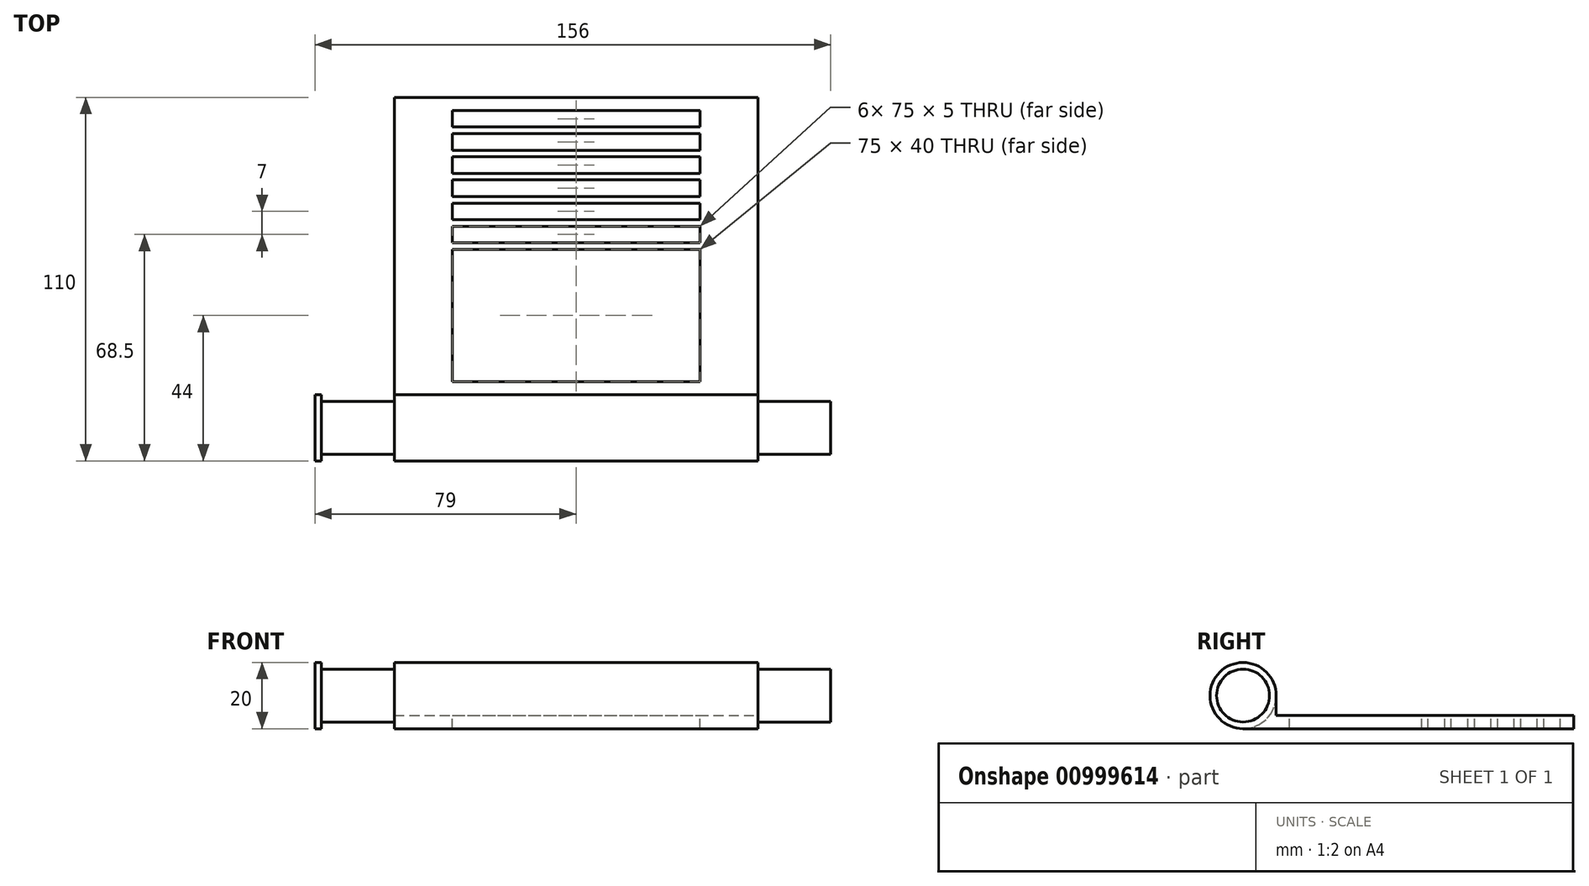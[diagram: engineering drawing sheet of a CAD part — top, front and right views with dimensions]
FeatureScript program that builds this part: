
annotation { "Feature Type Name" : "Feature", "Feature Type Description" : "" }
export const myFeature = defineFeature(function(context is Context, id is Id, definition is map)
    precondition{}
    {
        {
            var Q0;
            Q0=qCreatedBy(makeId("Top.planeOp"),FACE);
            var sketch = newSketch(context, id + "F0", { "sketchPlane" : qUnion([Q0])});
            skLineSegment(sketch, "E0.bottom", {"start": v(75, -45) * mm, "end": v(-75, -45) * mm});
            skLineSegment(sketch, "E0.top", {"start": v(75, 45) * mm, "end": v(-75, 45) * mm});
            skLineSegment(sketch, "E0.left", {"start": v(75, -45) * mm, "end": v(75, 45) * mm});
            skLineSegment(sketch, "E0.right", {"start": v(-75, -45) * mm, "end": v(-75, 45) * mm});
            skPoint(sketch, "E0.middle", {"position": v(0, 0) * mm});
            skLineSegment(sketch, "E1", {"start": v(-75, -45) * mm, "end": v(-75, -65) * mm});
            skLineSegment(sketch, "E2", {"start": v(-75, -65) * mm, "end": v(75, -65) * mm});
            skLineSegment(sketch, "E3", {"start": v(75, -65) * mm, "end": v(75, -45) * mm});
            skLineSegment(sketch, "E4", {"start": v(-55, -45) * mm, "end": v(-55, -65) * mm});
            skLineSegment(sketch, "E5", {"start": v(55, -45) * mm, "end": v(55, -65) * mm});
            skLineSegment(sketch, "E6", {"start": v(-55, -45) * mm, "end": v(-55, 45) * mm});
            skLineSegment(sketch, "E7", {"start": v(55, -45) * mm, "end": v(55, 45) * mm});
            skSolve(sketch);
        }
        {
            var Q0;
            {var subQ0=sQuery(id+"F0.wireOp",EDGE,"E4");Q0=makeQuery(id+"F0.imprint","IMPRINT",FACE,{"disambiguationData":[TD([[makeQuery(id+"F0.imprint","IMPRINT",EDGE,{"derivedFrom":subQ0}),1.0]])]});}
            var Q1;
            {var subQ0=sQuery(id+"F0.wireOp",EDGE,"E6");Q1=makeQuery(id+"F0.imprint","IMPRINT",FACE,{"disambiguationData":[TD([[makeQuery(id+"F0.imprint","IMPRINT",EDGE,{"derivedFrom":subQ0}),-1.0]])]});}
            extrude(context, id + "F1", {"entities" : qUnion([Q0, Q1]), "depth" : 4 * mm, "offsetDistance" : 25 * mm});
        }
        {
            var Q0;
            {var subQ0=sQuery(id+"F0.wireOp",EDGE,"E4");Q0=makeQuery(id+"F0.imprint","IMPRINT",FACE,{"disambiguationData":[TD([[makeQuery(id+"F0.imprint","IMPRINT",EDGE,{"derivedFrom":subQ0}),1.0]])]});}
            extrude(context, id + "F2", {"entities" : qUnion([Q0]), "operationType" : NewBodyOperationType.ADD, "depth" : 20 * mm, "offsetDistance" : 25 * mm});
        }
        {
            var Q0;
            Q0=qCreatedBy(makeId("Right.planeOp"),FACE);
            var sketch = newSketch(context, id + "F3", { "sketchPlane" : qUnion([Q0])});
            skLineSegment(sketch, "E8.0.0", {"start": v(-65, 0) * mm, "end": v(-65, 0) * mm});
            skLineSegment(sketch, "E8.0.1", {"start": v(-65, 0) * mm, "end": v(-65, 20) * mm});
            skLineSegment(sketch, "E8.0.2", {"start": v(-65, 20) * mm, "end": v(-45, 20) * mm});
            skLineSegment(sketch, "E8.0.3", {"start": v(-45, 20) * mm, "end": v(-45, 2) * mm});
            skLineSegment(sketch, "E8.0.4", {"start": v(-65, 0) * mm, "end": v(-65, 2) * mm});
            skPoint(sketch, "E9.centerSnap0", {"position": v(-45, 11) * mm});
            skPoint(sketch, "E9.centerSnap1", {"position": v(-55, 20) * mm});
            skCircle(sketch, "E10", {"center": v(-55, 10) * mm, "radius": 10 * mm});
            skPoint(sketch, "E10.centerSnap0", {"position": v(-65, 10) * mm});
            skCircle(sketch, "E11", {"center": v(-55, 10) * mm, "radius": 8 * mm});
            skLineSegment(sketch, "E12", {"start": v(-65, 0) * mm, "end": v(-41.71, 0) * mm});
            skLineSegment(sketch, "E13", {"start": v(-45, 2) * mm, "end": v(-45, 0) * mm});
            skSolve(sketch);
        }
        {
            var Q0;
            {var subQ0=sQuery(id+"F3.wireOp",EDGE,"E8.0.3");var subQ1=sQuery(id+"F3.wireOp",EDGE,"E8.0.2");var subQ2=makeQuery(id+"F3.imprint","INTERSECT",VERTEX,{"derivedFrom":[subQ1,subQ0]});Q0=makeQuery(id+"F3.imprint","IMPRINT",FACE,{"disambiguationData":[TD([[makeQuery(id+"F3.imprint","IMPRINT",EDGE,{"disambiguationData":[TD([[subQ2,1.0]])],"derivedFrom":subQ1}),-1.0]])]});}
            var Q1;
            {var subQ0=sQuery(id+"F3.wireOp",EDGE,"E10");var subQ1=sQuery(id+"F3.wireOp",EDGE,"E8.0.1");var subQ2=makeQuery(id+"F3.imprint","INTERSECT",VERTEX,{"derivedFrom":[subQ1,subQ0]});Q1=makeQuery(id+"F3.imprint","IMPRINT",FACE,{"disambiguationData":[TD([[makeQuery(id+"F3.imprint","IMPRINT",EDGE,{"disambiguationData":[TD([[subQ2,-1.0]])],"derivedFrom":subQ1}),-1.0]])]});}
            var Q2;
            {var subQ1=sQuery(id+"F3.wireOp",EDGE,"E8.0.1");var subQ3=makeQuery(id+"F3.imprint","IMPRINT",VERTEX,{"derivedFrom":subQ1});Q2=makeQuery(id+"F3.imprint","IMPRINT",FACE,{"disambiguationData":[TD([[makeQuery(id+"F3.imprint","IMPRINT",EDGE,{"disambiguationData":[TD([[subQ3,-1.0]])],"derivedFrom":subQ1}),-1.0]])]});}
            extrude(context, id + "F4", {"entities" : qUnion([Q0, Q1, Q2]), "operationType" : NewBodyOperationType.REMOVE, "endBound" : BoundingType.SYMMETRIC, "oppositeDirection" : true, "depth" : 200 * mm, "offsetDistance" : 25 * mm});
        }
        {
            var Q0;
            Q0=makeQuery(id+"F3.imprint","IMPRINT",FACE,{"disambiguationData":[TD([[makeQuery(id+"F3.imprint","IMPRINT",EDGE,{"derivedFrom":sQuery(id+"F3.wireOp",EDGE,"E11")}),1.0]])]});
            extrude(context, id + "F5", {"entities" : qUnion([Q0]), "operationType" : NewBodyOperationType.ADD, "endBound" : BoundingType.SYMMETRIC, "depth" : 154 * mm, "offsetDistance" : 25 * mm});
        }
        {
            var Q0;
            Q0=makeQuery(id+"F5.opExtrude","CAP_FACE",FACE,{"disambiguationData":[OSD([sQuery(id+"F3.wireOp",EDGE,"E11")])],"isStart":true});
            var sketch = newSketch(context, id + "F6", { "sketchPlane" : qUnion([Q0])});
            skCircle(sketch, "E14", {"center": v(55, 10) * mm, "radius": 10 * mm});
            skSolve(sketch);
        }
        {
            var Q0;
            Q0=makeQuery(id+"F6.imprint","IMPRINT",FACE,{"disambiguationData":[TD([[makeQuery(id+"F6.imprint","IMPRINT",EDGE,{"derivedFrom":sQuery(id+"F6.wireOp",EDGE,"E14")}),1.0]])]});
            var Q1;
            Q1=makeQuery(id+"F6.imprint","IMPRINT",FACE,{"disambiguationData":[TD([[makeQuery(id+"F6.imprint","IMPRINT",EDGE,{"derivedFrom":makeQuery(id+"F5.opExtrude","CAP_EDGE",EDGE,{"disambiguationData":[OSD([sQuery(id+"F3.wireOp",EDGE,"E11")])],"isStart":true})}),-1.0]])]});
            extrude(context, id + "F7", {"entities" : qUnion([Q0, Q1]), "operationType" : NewBodyOperationType.ADD, "depth" : 2 * mm, "offsetDistance" : 25 * mm});
        }
        {
            var Q0;
            Q0=makeQuery(id+"F1.opExtrude","CAP_FACE",FACE,{"disambiguationData":[OSD([sQuery(id+"F0.wireOp",EDGE,"E0.top"),sQuery(id+"F0.wireOp",EDGE,"E2"),sQuery(id+"F0.wireOp",EDGE,"E4"),sQuery(id+"F0.wireOp",EDGE,"E5"),sQuery(id+"F0.wireOp",EDGE,"E6"),sQuery(id+"F0.wireOp",EDGE,"E7")])],"isStart":false});
            var sketch = newSketch(context, id + "F8", { "sketchPlane" : qUnion([Q0])});
            skLineSegment(sketch, "E15", {"start": v(0, 45) * mm, "end": v(0, -45) * mm, "construction": true});
            skLineSegment(sketch, "E16.bottom", {"start": v(-37.5, 36) * mm, "end": v(37.5, 36) * mm});
            skLineSegment(sketch, "E16.top", {"start": v(-37.5, 41) * mm, "end": v(37.5, 41) * mm});
            skLineSegment(sketch, "E16.left", {"start": v(-37.5, 36) * mm, "end": v(-37.5, 41) * mm});
            skLineSegment(sketch, "E16.right", {"start": v(37.5, 36) * mm, "end": v(37.5, 41) * mm});
            skPoint(sketch, "E16.middle", {"position": v(0, 38.5) * mm});
            skLineSegment(sketch, "E17.0.1.0", {"start": v(-37.5, 34) * mm, "end": v(37.5, 34) * mm});
            skLineSegment(sketch, "E17.0.1.1", {"start": v(-37.5, 29) * mm, "end": v(37.5, 29) * mm});
            skLineSegment(sketch, "E17.0.1.2", {"start": v(37.5, 29) * mm, "end": v(37.5, 34) * mm});
            skLineSegment(sketch, "E17.0.1.3", {"start": v(-37.5, 29) * mm, "end": v(-37.5, 34) * mm});
            skLineSegment(sketch, "E17.0.2.0", {"start": v(-37.5, 27) * mm, "end": v(37.5, 27) * mm});
            skLineSegment(sketch, "E17.0.2.1", {"start": v(-37.5, 22) * mm, "end": v(37.5, 22) * mm});
            skLineSegment(sketch, "E17.0.2.2", {"start": v(37.5, 22) * mm, "end": v(37.5, 27) * mm});
            skLineSegment(sketch, "E17.0.2.3", {"start": v(-37.5, 22) * mm, "end": v(-37.5, 27) * mm});
            skLineSegment(sketch, "E17.0.3.0", {"start": v(-37.5, 20) * mm, "end": v(37.5, 20) * mm});
            skLineSegment(sketch, "E17.0.3.1", {"start": v(-37.5, 15) * mm, "end": v(37.5, 15) * mm});
            skLineSegment(sketch, "E17.0.3.2", {"start": v(37.5, 15) * mm, "end": v(37.5, 20) * mm});
            skLineSegment(sketch, "E17.0.3.3", {"start": v(-37.5, 15) * mm, "end": v(-37.5, 20) * mm});
            skLineSegment(sketch, "E17.0.4.0", {"start": v(-37.5, 13) * mm, "end": v(37.5, 13) * mm});
            skLineSegment(sketch, "E17.0.4.1", {"start": v(-37.5, 8) * mm, "end": v(37.5, 8) * mm});
            skLineSegment(sketch, "E17.0.4.2", {"start": v(37.5, 8) * mm, "end": v(37.5, 13) * mm});
            skLineSegment(sketch, "E17.0.4.3", {"start": v(-37.5, 8) * mm, "end": v(-37.5, 13) * mm});
            skLineSegment(sketch, "E17.direction1", {"start": v(37.5, 36) * mm, "end": v(60, 36) * mm, "construction": true});
            skLineSegment(sketch, "E17.direction2", {"start": v(37.5, 29) * mm, "end": v(37.5, 36) * mm, "construction": true});
            skLineSegment(sketch, "E18.0.0.5", {"start": v(-37.5, 6) * mm, "end": v(37.5, 6) * mm});
            skLineSegment(sketch, "E18.3.0.5", {"start": v(-37.5, 1) * mm, "end": v(37.5, 1) * mm});
            skLineSegment(sketch, "E18.6.0.5", {"start": v(37.5, 1) * mm, "end": v(37.5, 6) * mm});
            skLineSegment(sketch, "E18.9.0.5", {"start": v(-37.5, 1) * mm, "end": v(-37.5, 6) * mm});
            skLineSegment(sketch, "E18.6.0.6", {"start": v(37.5, -6) * mm, "end": v(37.5, -1) * mm});
            skLineSegment(sketch, "E18.9.0.6", {"start": v(-37.5, -6) * mm, "end": v(-37.5, -1) * mm});
            skLineSegment(sketch, "E18.6.0.7", {"start": v(37.5, -13) * mm, "end": v(37.5, -8) * mm});
            skLineSegment(sketch, "E18.9.0.7", {"start": v(-37.5, -13) * mm, "end": v(-37.5, -8) * mm});
            skLineSegment(sketch, "E18.6.0.8", {"start": v(37.5, -20) * mm, "end": v(37.5, -15) * mm});
            skLineSegment(sketch, "E18.9.0.8", {"start": v(-37.5, -20) * mm, "end": v(-37.5, -15) * mm});
            skLineSegment(sketch, "E18.6.0.9", {"start": v(37.5, -27) * mm, "end": v(37.5, -22) * mm});
            skLineSegment(sketch, "E18.9.0.9", {"start": v(-37.5, -27) * mm, "end": v(-37.5, -22) * mm});
            skLineSegment(sketch, "E18.6.0.10", {"start": v(37.5, -34) * mm, "end": v(37.5, -29) * mm});
            skLineSegment(sketch, "E18.9.0.10", {"start": v(-37.5, -34) * mm, "end": v(-37.5, -29) * mm});
            skLineSegment(sketch, "E18.3.0.11", {"start": v(-37.5, -41) * mm, "end": v(37.5, -41) * mm});
            skLineSegment(sketch, "E18.6.0.11", {"start": v(37.5, -41) * mm, "end": v(37.5, -36) * mm});
            skLineSegment(sketch, "E18.9.0.11", {"start": v(-37.5, -41) * mm, "end": v(-37.5, -36) * mm});
            skLineSegment(sketch, "E19", {"start": v(-47, 45) * mm, "end": v(-47, 31) * mm, "construction": true});
            skPoint(sketch, "E20.middle", {"position": v(-47, 31) * mm});
            skLineSegment(sketch, "E21", {"start": v(37.5, -36) * mm, "end": v(37.5, -34) * mm});
            skLineSegment(sketch, "E22", {"start": v(-37.5, -36) * mm, "end": v(-37.5, -34) * mm});
            skLineSegment(sketch, "E23", {"start": v(-37.5, -41) * mm, "end": v(-37.5, -1) * mm});
            skLineSegment(sketch, "E24", {"start": v(-37.5, -1) * mm, "end": v(37.5, -1) * mm});
            skLineSegment(sketch, "E25", {"start": v(37.5, -41) * mm, "end": v(37.5, -1) * mm});
            skSolve(sketch);
        }
        {
            var Q0;
            Q0=makeQuery(id+"F8.imprint","IMPRINT",FACE,{"disambiguationData":[TD([[makeQuery(id+"F8.imprint","IMPRINT",EDGE,{"derivedFrom":sQuery(id+"F8.wireOp",EDGE,"E18.0.0.11")}),-1.0]])]});
            var Q1;
            Q1=makeQuery(id+"F8.imprint","IMPRINT",FACE,{"disambiguationData":[TD([[makeQuery(id+"F8.imprint","IMPRINT",EDGE,{"derivedFrom":sQuery(id+"F8.wireOp",EDGE,"E18.0.0.5")}),-1.0]])]});
            var Q2;
            Q2=makeQuery(id+"F8.imprint","IMPRINT",FACE,{"disambiguationData":[TD([[makeQuery(id+"F8.imprint","IMPRINT",EDGE,{"derivedFrom":sQuery(id+"F8.wireOp",EDGE,"E17.0.4.0")}),-1.0]])]});
            var Q3;
            Q3=makeQuery(id+"F8.imprint","IMPRINT",FACE,{"disambiguationData":[TD([[makeQuery(id+"F8.imprint","IMPRINT",EDGE,{"derivedFrom":sQuery(id+"F8.wireOp",EDGE,"E17.0.1.0")}),-1.0]])]});
            var Q4;
            Q4=makeQuery(id+"F8.imprint","IMPRINT",FACE,{"disambiguationData":[TD([[makeQuery(id+"F8.imprint","IMPRINT",EDGE,{"derivedFrom":sQuery(id+"F8.wireOp",EDGE,"E17.0.2.0")}),-1.0]])]});
            var Q5;
            Q5=makeQuery(id+"F8.imprint","IMPRINT",FACE,{"disambiguationData":[TD([[makeQuery(id+"F8.imprint","IMPRINT",EDGE,{"derivedFrom":sQuery(id+"F8.wireOp",EDGE,"E17.0.3.0")}),-1.0]])]});
            var Q6;
            Q6=makeQuery(id+"F8.imprint","IMPRINT",FACE,{"disambiguationData":[TD([[makeQuery(id+"F8.imprint","IMPRINT",EDGE,{"derivedFrom":sQuery(id+"F8.wireOp",EDGE,"E16.bottom")}),1.0]])]});
            var Q7;
            Q7=makeQuery(id+"F8.imprint","IMPRINT",FACE,{"disambiguationData":[TD([[makeQuery(id+"F8.imprint","IMPRINT",EDGE,{"derivedFrom":sQuery(id+"F8.wireOp",EDGE,"E18.3.0.10")}),-1.0]])]});
            var Q8;
            {var subQ0=sQuery(id+"F8.wireOp",EDGE,"E18.3.0.11");Q8=makeQuery(id+"F8.imprint","IMPRINT",FACE,{"disambiguationData":[TD([[makeQuery(id+"F8.imprint","IMPRINT",EDGE,{"derivedFrom":subQ0}),1.0]])]});}
            extrude(context, id + "F9", {"entities" : qUnion([Q0, Q1, Q2, Q3, Q4, Q5, Q6, Q7, Q8]), "operationType" : NewBodyOperationType.REMOVE, "oppositeDirection" : true, "depth" : 25 * mm, "offsetDistance" : 25 * mm});
        }
    });
